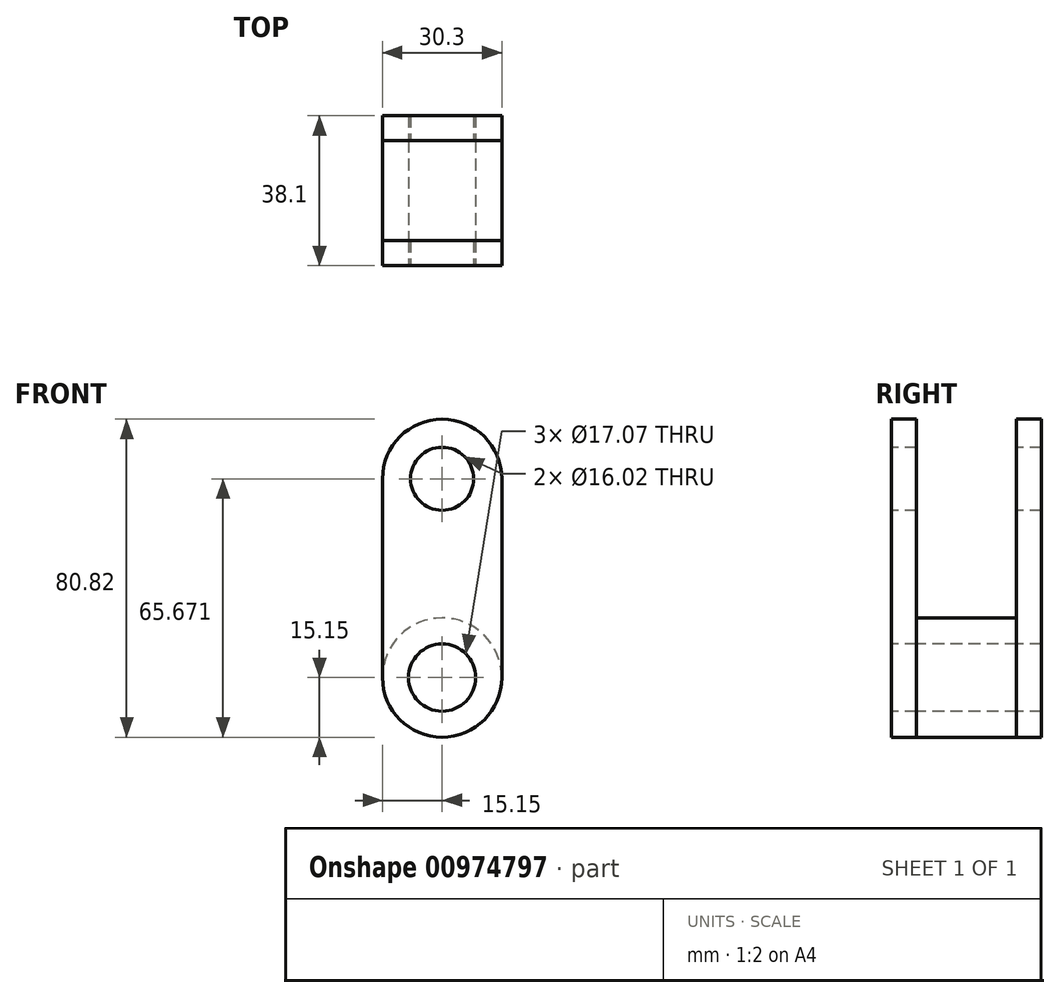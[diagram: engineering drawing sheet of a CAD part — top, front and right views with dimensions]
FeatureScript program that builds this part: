
annotation { "Feature Type Name" : "Feature", "Feature Type Description" : "" }
export const myFeature = defineFeature(function(context is Context, id is Id, definition is map)
    precondition{}
    {
        {
            var Q0;
            Q0=qCreatedBy(makeId("Front.planeOp"),FACE);
            var sketch = newSketch(context, id + "F0", { "sketchPlane" : qUnion([Q0])});
            skCircle(sketch, "E0", {"center": v(0, 0) * mm, "radius": 15.15 * mm});
            skCircle(sketch, "E1", {"center": v(0, 50.52) * mm, "radius": 15.15 * mm});
            skLineSegment(sketch, "E2", {"start": v(15.15, 0) * mm, "end": v(15.15, 50.52) * mm});
            skLineSegment(sketch, "E3", {"start": v(-15.15, 0) * mm, "end": v(-15.15, 50.52) * mm});
            skSolve(sketch);
        }
        {
            var Q0;
            {var subQ0=sQuery(id+"F0.wireOp",EDGE,"E1");var subQ1=makeQuery(id+"F0.imprint","INTERSECT",VERTEX,{"derivedFrom":[subQ0,sQuery(id+"F0.wireOp",EDGE,"E2")]});Q0=makeQuery(id+"F0.imprint","IMPRINT",FACE,{"disambiguationData":[TD([[makeQuery(id+"F0.imprint","IMPRINT",EDGE,{"disambiguationData":[TD([[subQ1,-1.0]])],"derivedFrom":subQ0}),1.0]])]});}
            var Q1;
            {var subQ0=sQuery(id+"F0.wireOp",EDGE,"E2");Q1=makeQuery(id+"F0.imprint","IMPRINT",FACE,{"disambiguationData":[TD([[makeQuery(id+"F0.imprint","IMPRINT",EDGE,{"derivedFrom":subQ0}),1.0]])]});}
            var Q2;
            {var subQ0=sQuery(id+"F0.wireOp",EDGE,"E0");var subQ1=makeQuery(id+"F0.imprint","INTERSECT",VERTEX,{"derivedFrom":[subQ0,sQuery(id+"F0.wireOp",EDGE,"E2")]});Q2=makeQuery(id+"F0.imprint","IMPRINT",FACE,{"disambiguationData":[TD([[makeQuery(id+"F0.imprint","IMPRINT",EDGE,{"disambiguationData":[TD([[subQ1,-1.0]])],"derivedFrom":subQ0}),1.0]])]});}
            extrude(context, id + "F1", {"entities" : qUnion([Q0, Q1, Q2]), "depth" : 6.35 * mm, "offsetDistance" : 25.4 * mm});
        }
        {
            var Q0;
            {var subQ0=sQuery(id+"F0.wireOp",EDGE,"E0");var subQ1=makeQuery(id+"F0.imprint","INTERSECT",VERTEX,{"derivedFrom":[subQ0,sQuery(id+"F0.wireOp",EDGE,"E2")]});Q0=makeQuery(id+"F0.imprint","IMPRINT",FACE,{"disambiguationData":[TD([[makeQuery(id+"F0.imprint","IMPRINT",EDGE,{"disambiguationData":[TD([[subQ1,-1.0]])],"derivedFrom":subQ0}),1.0]])]});}
            var Q1;
            {var subQ0=sQuery(id+"F0.wireOp",EDGE,"E2");Q1=makeQuery(id+"F0.imprint","IMPRINT",FACE,{"disambiguationData":[TD([[makeQuery(id+"F0.imprint","IMPRINT",EDGE,{"derivedFrom":subQ0}),1.0]])]});}
            var Q2;
            {var subQ0=sQuery(id+"F0.wireOp",EDGE,"E1");var subQ1=makeQuery(id+"F0.imprint","INTERSECT",VERTEX,{"derivedFrom":[subQ0,sQuery(id+"F0.wireOp",EDGE,"E2")]});Q2=makeQuery(id+"F0.imprint","IMPRINT",FACE,{"disambiguationData":[TD([[makeQuery(id+"F0.imprint","IMPRINT",EDGE,{"disambiguationData":[TD([[subQ1,-1.0]])],"derivedFrom":subQ0}),1.0]])]});}
            extrude(context, id + "F2", {"entities" : qUnion([Q0, Q1, Q2]), "operationType" : NewBodyOperationType.ADD, "oppositeDirection" : true, "depth" : 31.75 * mm, "offsetDistance" : 25.4 * mm});
        }
        {
            var Q0;
            Q0 = qSketchRegion(id + "F0", true);
            extrude(context, id + "F3", {"entities" : qUnion([Q0]), "operationType" : NewBodyOperationType.REMOVE, "oppositeDirection" : true, "depth" : 25.4 * mm, "offsetDistance" : 25.4 * mm});
        }
        {
            var Q0;
            {var subQ0=sQuery(id+"F0.wireOp",EDGE,"E0");var subQ1=makeQuery(id+"F0.imprint","INTERSECT",VERTEX,{"derivedFrom":[subQ0,sQuery(id+"F0.wireOp",EDGE,"E2")]});Q0=makeQuery(id+"F0.imprint","IMPRINT",FACE,{"disambiguationData":[TD([[makeQuery(id+"F0.imprint","IMPRINT",EDGE,{"disambiguationData":[TD([[subQ1,-1.0]])],"derivedFrom":subQ0}),1.0]])]});}
            extrude(context, id + "F4", {"entities" : qUnion([Q0]), "oppositeDirection" : true, "depth" : 25.4 * mm, "offsetDistance" : 25.4 * mm});
        }
        {
            var Q0;
            Q0=makeQuery(id+"F1.opExtrude","CAP_FACE",FACE,{"disambiguationData":[OSD([sQuery(id+"F0.wireOp",EDGE,"E0"),sQuery(id+"F0.wireOp",EDGE,"E1"),sQuery(id+"F0.wireOp",EDGE,"E2"),sQuery(id+"F0.wireOp",EDGE,"E3")])],"isStart":false});
            var sketch = newSketch(context, id + "F5", { "sketchPlane" : qUnion([Q0])});
            skCircle(sketch, "E4", {"center": v(0, 50.52) * mm, "radius": 8 * mm});
            skCircle(sketch, "E5", {"center": v(0, 0) * mm, "radius": 8.53 * mm});
            skSolve(sketch);
        }
        {
            var Q0;
            Q0 = qSketchRegion(id + "F5", true);
            extrude(context, id + "F6", {"entities" : qUnion([Q0]), "operationType" : NewBodyOperationType.REMOVE, "endBound" : BoundingType.THROUGH_ALL, "oppositeDirection" : true, "depth" : 25.4 * mm, "offsetDistance" : 25.4 * mm});
        }
    });
